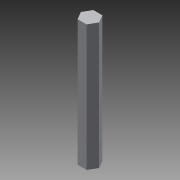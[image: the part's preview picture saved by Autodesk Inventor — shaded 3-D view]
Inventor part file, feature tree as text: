
AUTODESK INVENTOR PART (.ipt)
format: ipt  version: 2013 (Build 170138000, 138)  size: 69,120 bytes
history: native  units: in
note: dims shown in document units (in); Inventor stores cm internally (conversion verified against a paired STEP export)
features: extrude x1, sketch x1
ambient origin geometry x8: Origin, YZ Plane, XZ Plane, XY Plane, X Axis, Y Axis, Z Axis, Center Point
bodies: Solid1 (feature_tree)
feature tree (2):
  extrude  "Extrusion1"  Depth=3.0in TaperAngle=0.0deg
  sketch  "Sketch1"  dims[d0=0.375in d1=3.0in d2=0.0in]
